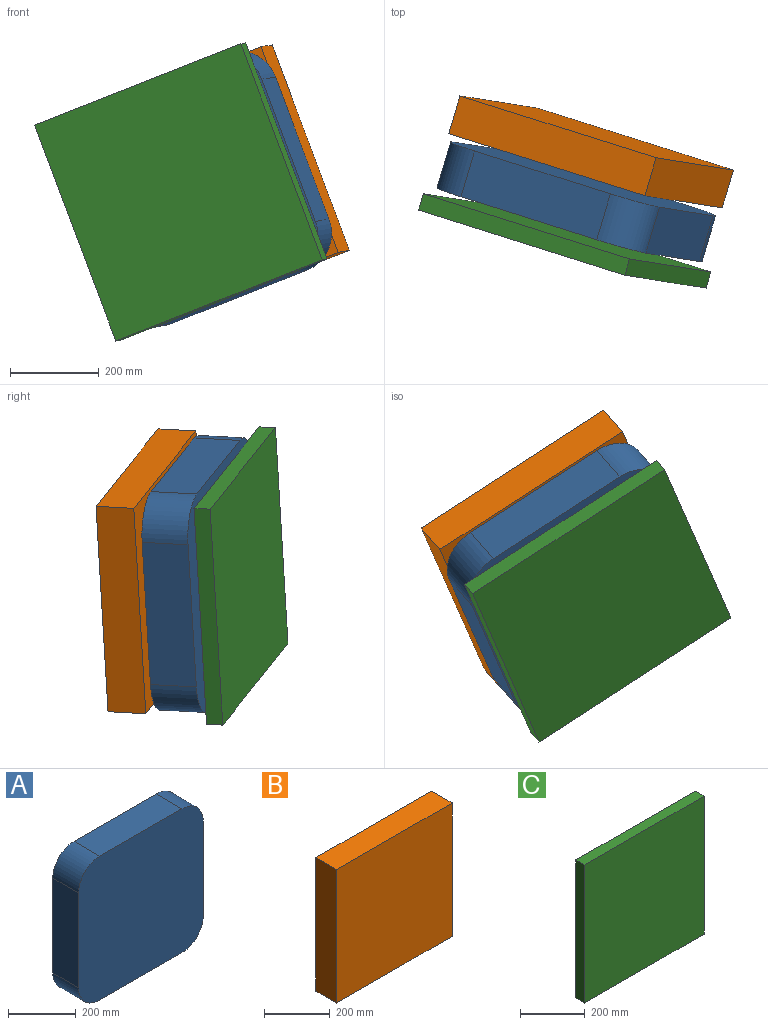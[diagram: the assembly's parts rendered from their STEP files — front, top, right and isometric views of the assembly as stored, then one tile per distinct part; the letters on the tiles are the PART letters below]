
ASSEMBLY  parts=3 mates=2
PART A: 10 faces, bbox 520.7x108x520.7 mm
  f0: plane 342.9x107.95mm, normal (-1,0,0), area 37016.1mm2, adj f4,f5,f6,f9
  f1: plane 342.9x107.95mm, normal (0,0,-1), area 37016.1mm2, adj f4,f5,f6,f7
  f2: plane 342.9x107.95mm, normal (1,0,0), area 37016.1mm2, adj f4,f5,f7,f8
  f3: plane 342.9x107.95mm, normal (0,0,1), area 37016.1mm2, adj f4,f5,f8,f9
  f4: plane 520.7x520.7mm, normal (0,1,0), area 264344.3mm2, adj f0,f1,f2,f3,f6,f7,f8,f9
  f5: plane 520.7x520.7mm, normal (0,-1,0), area 264344.3mm2, adj f0,f1,f2,f3,f6,f7,f8,f9
  f6: cylinder r=88.9mm len=107.95mm, axis (0,-1,0), area 15074.5mm2, adj f0,f1,f4,f5
  f7: cylinder r=88.9mm len=107.95mm, axis (0,-1,0), area 15074.5mm2, adj f1,f2,f4,f5
  f8: cylinder r=88.9mm len=107.95mm, axis (0,-1,0), area 15074.5mm2, adj f2,f3,f4,f5
  f9: cylinder r=88.9mm len=107.95mm, axis (0,-1,0), area 15074.5mm2, adj f0,f3,f4,f5
PART B: 6 faces, bbox 495.3x88.9x495.3 mm
  f0: plane 495.3x88.9mm, normal (-1,0,0), area 44032.2mm2, adj f1,f3,f4,f5
  f1: plane 495.3x88.9mm, normal (0,0,1), area 44032.2mm2, adj f0,f2,f4,f5
  f2: plane 495.3x88.9mm, normal (1,0,0), area 44032.2mm2, adj f1,f3,f4,f5
  f3: plane 495.3x88.9mm, normal (0,0,-1), area 44032.2mm2, adj f0,f2,f4,f5
  f4: plane 495.3x495.3mm, normal (0,1,0), area 245322.1mm2, adj f0,f1,f2,f3
  f5: plane 495.3x495.3mm, normal (0,-1,0), area 245322.1mm2, adj f0,f1,f2,f3
PART C: 6 faces, bbox 520.7x38.1x520.7 mm
  f0: plane 520.7x38.1mm, normal (0,0,-1), area 19838.7mm2, adj f1,f3,f4,f5
  f1: plane 520.7x38.1mm, normal (1,0,0), area 19838.7mm2, adj f0,f2,f4,f5
  f2: plane 520.7x38.1mm, normal (0,0,1), area 19838.7mm2, adj f1,f3,f4,f5
  f3: plane 520.7x38.1mm, normal (-1,0,0), area 19838.7mm2, adj f0,f2,f4,f5
  f4: plane 520.7x520.7mm, normal (0,-1,0), area 271128.5mm2, adj f0,f1,f2,f3
  f5: plane 520.7x520.7mm, normal (0,1,0), area 271128.5mm2, adj f0,f1,f2,f3
PLACE A rot(axis=(0,-0.78,-0.63),26.8deg) t=(81.73,385.67,-108.9)mm
PLACE B rot(axis=(0,-0.78,-0.63),26.8deg) t=(48.99,411.67,-41.2)mm
PLACE C rot(axis=(0,-0.78,-0.63),26.8deg) t=(76.34,367.43,-109.86)mm
MATE slider A.f4 <-> B.f5  axis (0.28,0.96,0.05) through (45.04,510.05,-124.64)mm
MATE slider C.f5 <-> A.f5  axis (0.28,0.96,0.05) through (9.1,388.42,-131.05)mm
